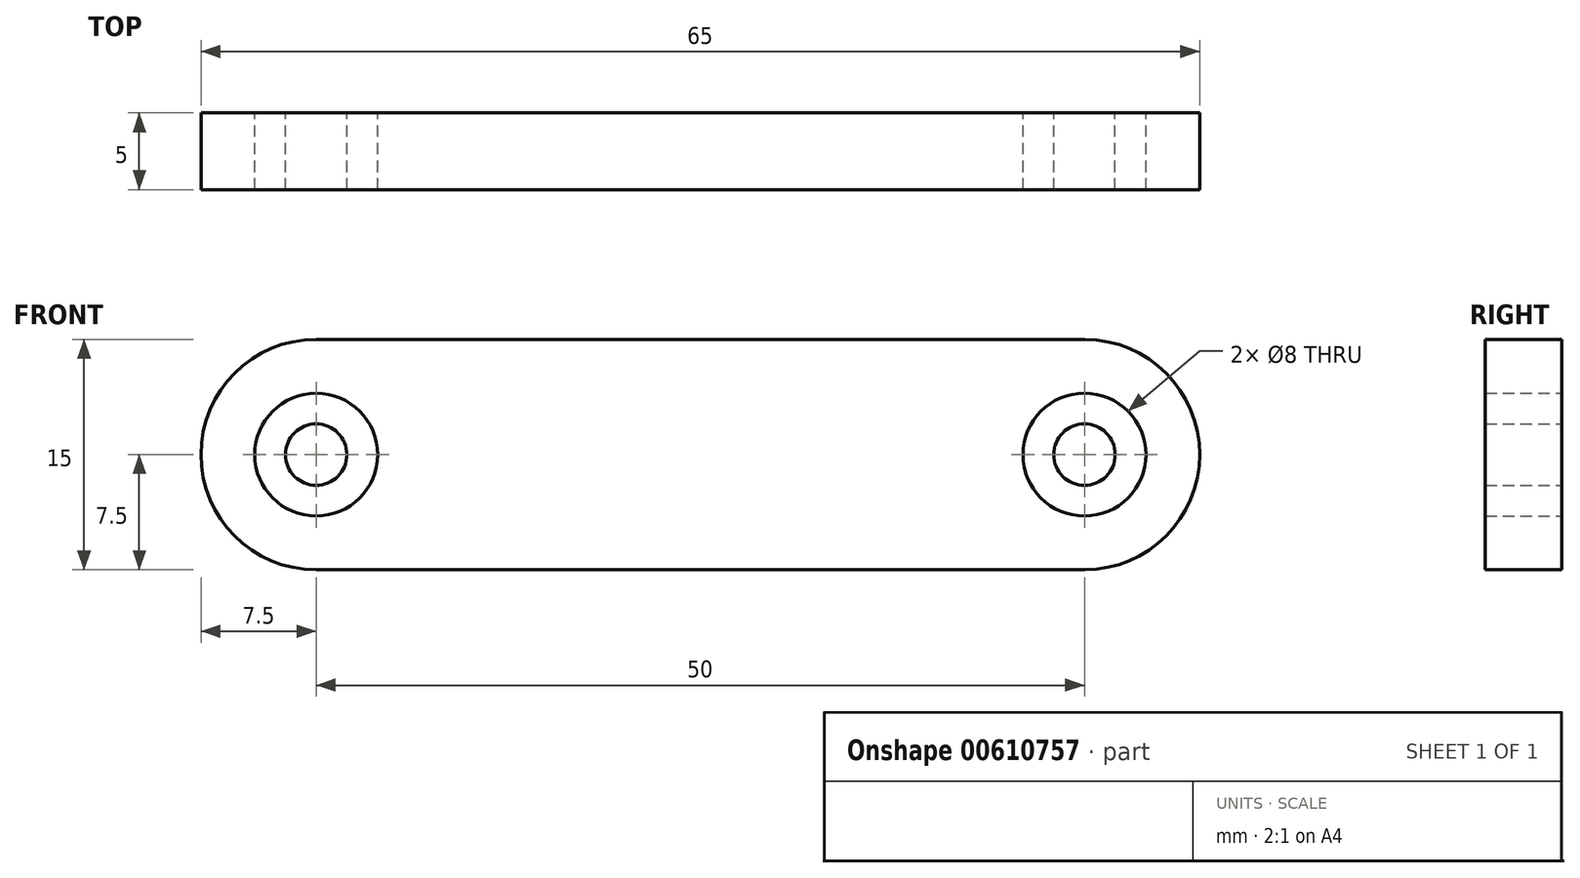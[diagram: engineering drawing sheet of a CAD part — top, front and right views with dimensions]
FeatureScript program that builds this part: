
annotation { "Feature Type Name" : "Feature", "Feature Type Description" : "" }
export const myFeature = defineFeature(function(context is Context, id is Id, definition is map)
    precondition{}
    {
        {
            var Q0;
            Q0=qCreatedBy(makeId("Front.planeOp"),FACE);
            var sketch = newSketch(context, id + "F0", { "sketchPlane" : qUnion([Q0])});
            skArc(sketch, "E0", {"start": v(0, 7.5) * mm, "mid": v(-7.5, 0) * mm, "end": v(0, -7.5) * mm});
            skArc(sketch, "E1", {"start": v(50, -7.5) * mm, "mid": v(57.5, 0) * mm, "end": v(50, 7.5) * mm});
            skLineSegment(sketch, "E2", {"start": v(0, 7.5) * mm, "end": v(50, 7.5) * mm});
            skLineSegment(sketch, "E3", {"start": v(0, -7.5) * mm, "end": v(50, -7.5) * mm});
            skCircle(sketch, "E4", {"center": v(0, 0) * mm, "radius": 4 * mm});
            skCircle(sketch, "E5", {"center": v(50, 0) * mm, "radius": 4 * mm});
            skSolve(sketch);
        }
        {
            var Q0;
            Q0 = qSketchRegion(id + "F0", true);
            extrude(context, id + "F1", {"entities" : qUnion([Q0]), "depth" : 5 * mm, "offsetDistance" : 25.4 * mm});
        }
        {
            var Q0;
            Q0=qCreatedBy(makeId("Front.planeOp"),FACE);
            var sketch = newSketch(context, id + "F2", { "sketchPlane" : qUnion([Q0])});
            skCircle(sketch, "E6", {"center": v(0, 0) * mm, "radius": 2 * mm});
            skLineSegment(sketch, "E7", {"start": v(50, 10.74) * mm, "end": v(50, -13.3) * mm, "construction": true});
            skLineSegment(sketch, "E8", {"start": v(41.74, 0) * mm, "end": v(57.27, 0) * mm, "construction": true});
            skCircle(sketch, "E9", {"center": v(50, 0) * mm, "radius": 2 * mm});
            skPoint(sketch, "E9.centerSnap0", {"position": v(50, -1.28) * mm});
            skSolve(sketch);
        }
        {
            var Q0;
            Q0=makeQuery(id+"F2.imprint","IMPRINT",FACE,{"disambiguationData":[TD([[makeQuery(id+"F2.imprint","IMPRINT",EDGE,{"derivedFrom":sQuery(id+"F2.wireOp",EDGE,"E6")}),1.0]])]});
            var Q1;
            Q1=makeQuery(id+"F2.imprint","IMPRINT",FACE,{"disambiguationData":[TD([[makeQuery(id+"F2.imprint","IMPRINT",EDGE,{"derivedFrom":sQuery(id+"F2.wireOp",EDGE,"E9")}),1.0]])]});
            extrude(context, id + "F3", {"entities" : qUnion([Q0, Q1]), "depth" : 5 * mm, "offsetDistance" : 25.4 * mm});
        }
    });
